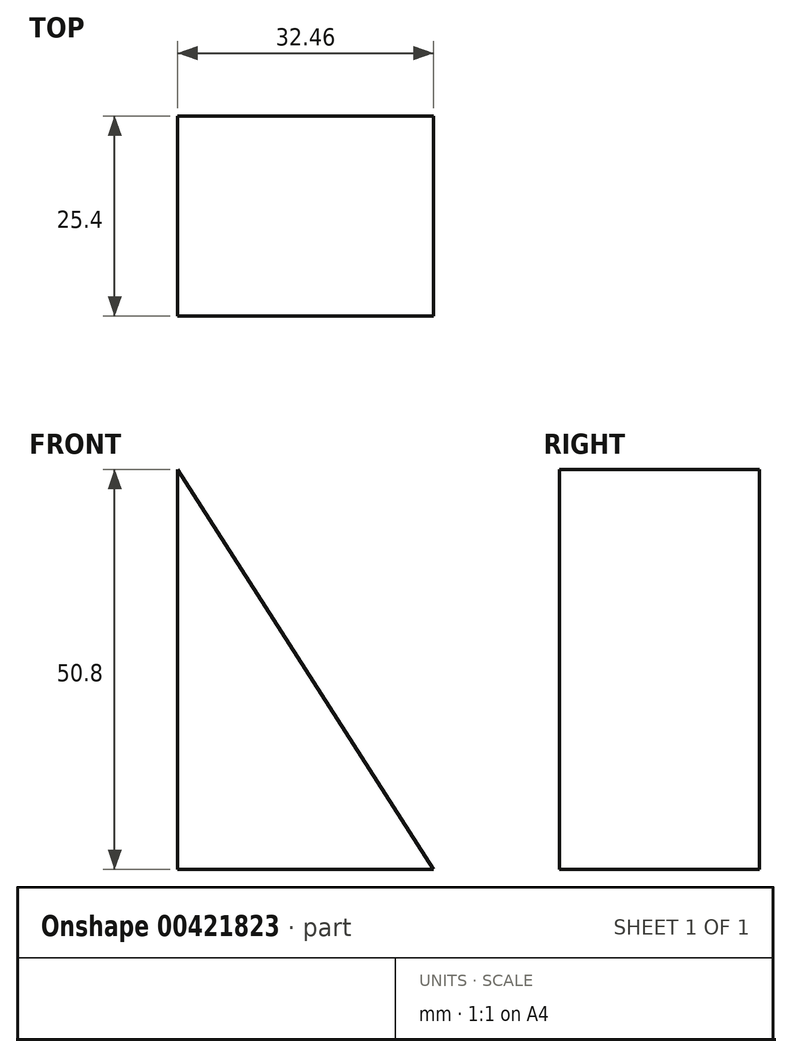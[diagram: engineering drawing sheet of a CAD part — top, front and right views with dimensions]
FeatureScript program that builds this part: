
annotation { "Feature Type Name" : "Feature", "Feature Type Description" : "" }
export const myFeature = defineFeature(function(context is Context, id is Id, definition is map)
    precondition{}
    {
        {
            var Q0;
            Q0=qCreatedBy(makeId("Front.planeOp"),FACE);
            var sketch = newSketch(context, id + "F0", { "sketchPlane" : qUnion([Q0])});
            skLineSegment(sketch, "E0", {"start": v(18.34, 0) * mm, "end": v(-32.46, 0) * mm});
            skLineSegment(sketch, "E1", {"start": v(-32.46, 0) * mm, "end": v(-32.46, 50.8) * mm});
            skLineSegment(sketch, "E2", {"start": v(-32.46, 50.8) * mm, "end": v(0, 0) * mm});
            skSolve(sketch);
        }
        {
            var Q0;
            Q0 = qSketchRegion(id + "F0", true);
            extrude(context, id + "F1", {"entities" : qUnion([Q0]), "depth" : 25.4 * mm});
        }
    });
